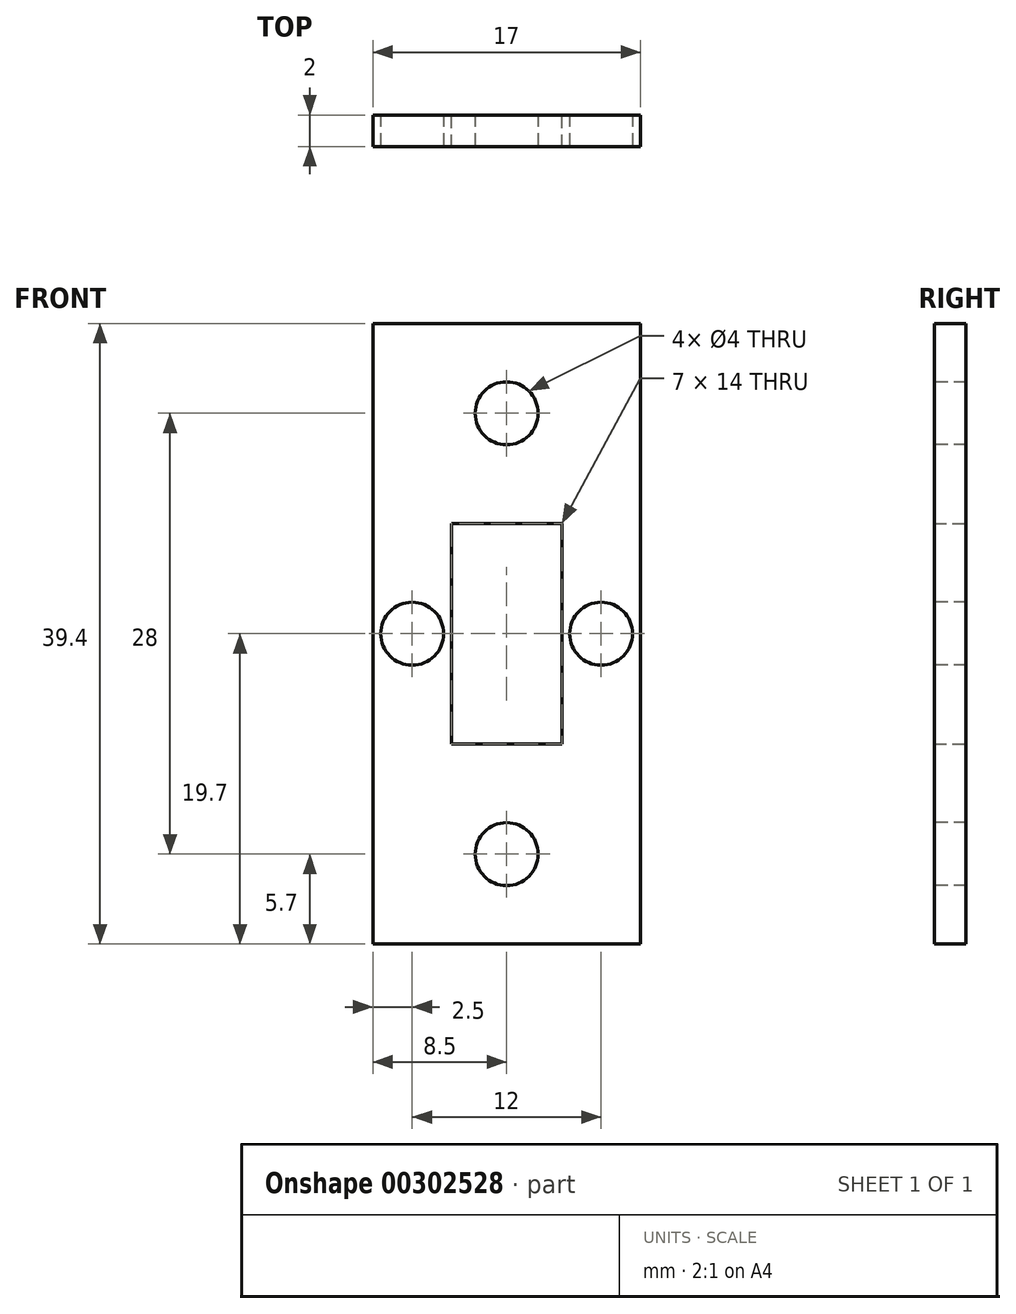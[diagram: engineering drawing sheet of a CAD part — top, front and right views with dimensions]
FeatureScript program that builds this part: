
annotation { "Feature Type Name" : "Feature", "Feature Type Description" : "" }
export const myFeature = defineFeature(function(context is Context, id is Id, definition is map)
    precondition{}
    {
        {
            var Q0;
            Q0=qCreatedBy(makeId("Front.planeOp"),FACE);
            var sketch = newSketch(context, id + "F0", { "sketchPlane" : qUnion([Q0])});
            skLineSegment(sketch, "E0.bottom", {"start": v(3.5, 7) * mm, "end": v(-3.5, 7) * mm});
            skLineSegment(sketch, "E0.top", {"start": v(3.5, -7) * mm, "end": v(-3.5, -7) * mm});
            skLineSegment(sketch, "E0.left", {"start": v(3.5, 7) * mm, "end": v(3.5, -7) * mm});
            skLineSegment(sketch, "E0.right", {"start": v(-3.5, 7) * mm, "end": v(-3.5, -7) * mm});
            skPoint(sketch, "E0.middle", {"position": v(0, 0) * mm});
            skLineSegment(sketch, "E1.bottom", {"start": v(8.5, 19.7) * mm, "end": v(-8.5, 19.7) * mm});
            skLineSegment(sketch, "E1.top", {"start": v(8.5, -19.7) * mm, "end": v(-8.5, -19.7) * mm});
            skLineSegment(sketch, "E1.left", {"start": v(8.5, 19.7) * mm, "end": v(8.5, -19.7) * mm});
            skLineSegment(sketch, "E1.right", {"start": v(-8.5, 19.7) * mm, "end": v(-8.5, -19.7) * mm});
            skSolve(sketch);
        }
        {
            var Q0;
            Q0=makeQuery(id+"F0.imprint","IMPRINT",FACE,{"disambiguationData":[TD([[makeQuery(id+"F0.imprint","IMPRINT",EDGE,{"derivedFrom":sQuery(id+"F0.wireOp",EDGE,"E0.bottom")}),-1.0]])]});
            extrude(context, id + "F1", {"entities" : qUnion([Q0]), "depth" : 2 * mm});
        }
        {
            var Q0;
            Q0=makeQuery(id+"F1.opExtrude","CAP_FACE",FACE,{"disambiguationData":[OSD([sQuery(id+"F0.wireOp",EDGE,"E0.bottom"),sQuery(id+"F0.wireOp",EDGE,"E0.top"),sQuery(id+"F0.wireOp",EDGE,"E0.left"),sQuery(id+"F0.wireOp",EDGE,"E0.right"),sQuery(id+"F0.wireOp",EDGE,"E1.bottom"),sQuery(id+"F0.wireOp",EDGE,"E1.top"),sQuery(id+"F0.wireOp",EDGE,"E1.left"),sQuery(id+"F0.wireOp",EDGE,"E1.right")])],"isStart":false});
            var sketch = newSketch(context, id + "F2", { "sketchPlane" : qUnion([Q0])});
            skPoint(sketch, "E2", {"position": v(-6, 0) * mm});
            skPoint(sketch, "E2.positionSnap0", {"position": v(-3.5, 0) * mm});
            skPoint(sketch, "E3", {"position": v(6, 0) * mm});
            skPoint(sketch, "E3.positionSnap0", {"position": v(3.5, 0) * mm});
            skPoint(sketch, "E4", {"position": v(0, 14) * mm});
            skPoint(sketch, "E4.positionSnap0", {"position": v(0, 7) * mm});
            skPoint(sketch, "E5", {"position": v(0, -14) * mm});
            skPoint(sketch, "E5.positionSnap0", {"position": v(0, -7) * mm});
            skSolve(sketch);
        }
        {
            var Q0;
            Q0=sQuery(id+"F2.wireOp",VERTEX,"E2");
            var Q1;
            Q1=sQuery(id+"F2.wireOp",VERTEX,"E3");
            var Q2;
            Q2=sQuery(id+"F2.wireOp",VERTEX,"E4");
            var Q3;
            Q3=sQuery(id+"F2.wireOp",VERTEX,"E5");
            var Q4;
            Q4=makeQuery(id+"F1.opExtrude","SWEPT_BODY",BODY,{"disambiguationData":[OSD([sQuery(id+"F0.wireOp",EDGE,"E0.bottom"),sQuery(id+"F0.wireOp",EDGE,"E0.top"),sQuery(id+"F0.wireOp",EDGE,"E0.left"),sQuery(id+"F0.wireOp",EDGE,"E0.right"),sQuery(id+"F0.wireOp",EDGE,"E1.bottom"),sQuery(id+"F0.wireOp",EDGE,"E1.top"),sQuery(id+"F0.wireOp",EDGE,"E1.left"),sQuery(id+"F0.wireOp",EDGE,"E1.right")])]});
            hole(context, id + "F3", {"style" : HoleStyle.SIMPLE, "endStyle" : HoleEndStyle.BLIND, "holeDiameter" : 4 * mm, "holeDepth" : 6 * mm, "isTappedThrough" : true, "tappedDepth" : 12 * mm, "tapClearance" : 3, "locations" : qUnion([Q0, Q1, Q2, Q3]), "scope" : qUnion([Q4])});
        }
    });
